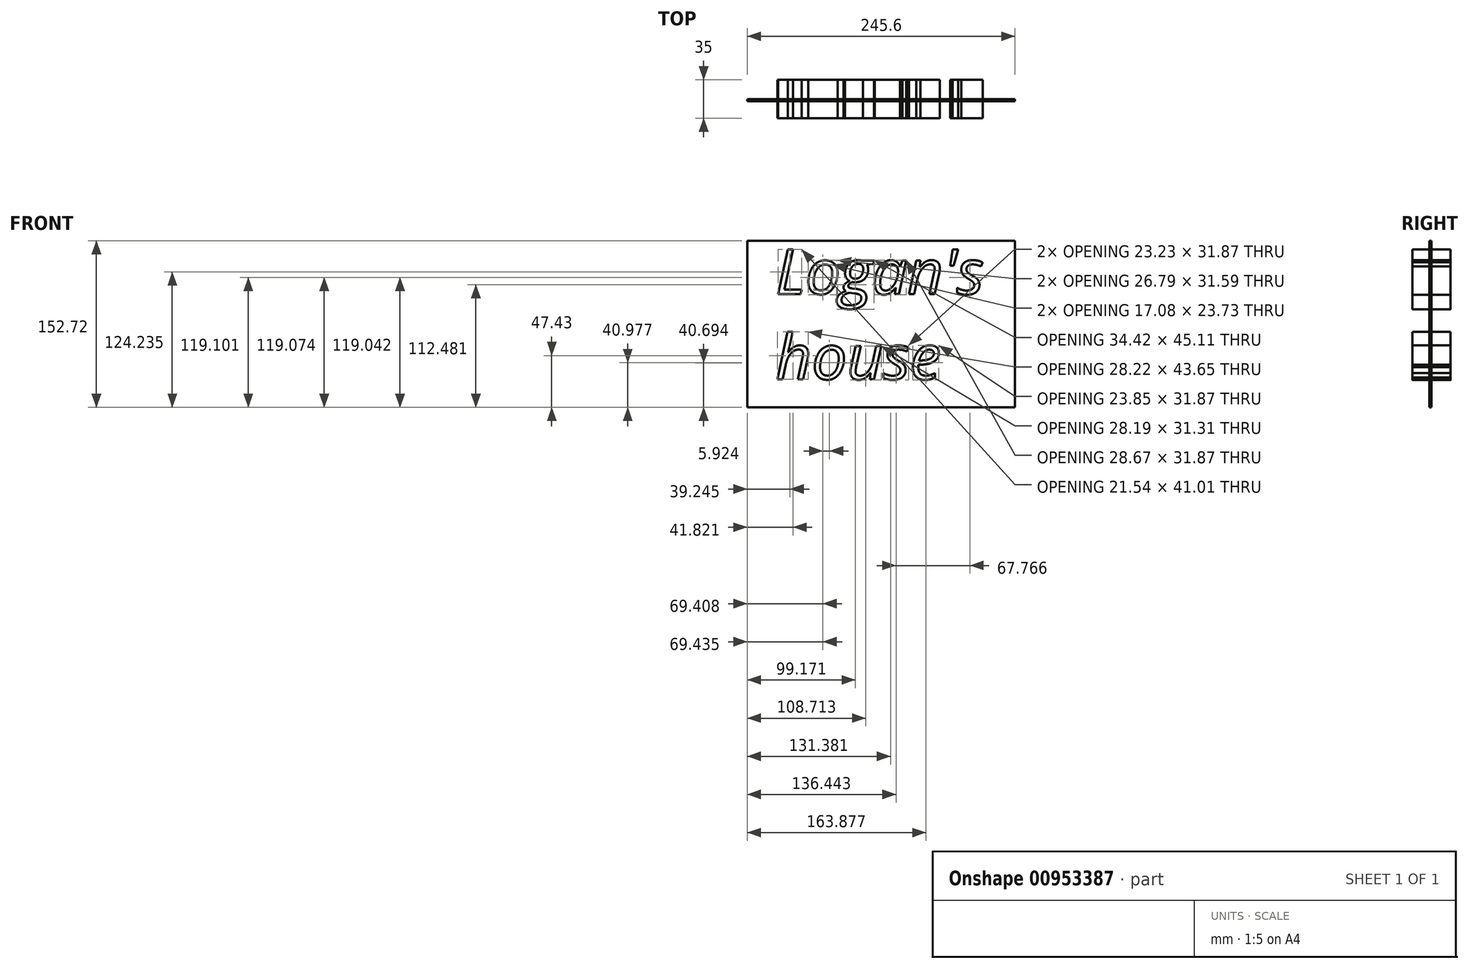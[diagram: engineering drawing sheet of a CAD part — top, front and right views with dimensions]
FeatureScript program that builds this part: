
annotation { "Feature Type Name" : "Feature", "Feature Type Description" : "" }
export const myFeature = defineFeature(function(context is Context, id is Id, definition is map)
    precondition{}
    {
        {
            var Q0;
            Q0=qCreatedBy(makeId("Front.planeOp"),FACE);
            var sketch = newSketch(context, id + "F0", { "sketchPlane" : qUnion([Q0])});
            skText(sketch, "E0", { "text": "Logan\'s \nhouse\n", "fontName": "OpenSans-Italic.ttf"});
            skLineSegment(sketch, "E1.bottom", {"start": v(122.8, -76.36) * mm, "end": v(-122.8, -76.36) * mm});
            skLineSegment(sketch, "E1.top", {"start": v(122.8, 76.36) * mm, "end": v(-122.8, 76.36) * mm});
            skLineSegment(sketch, "E1.left", {"start": v(122.8, -76.36) * mm, "end": v(122.8, 76.36) * mm});
            skLineSegment(sketch, "E1.right", {"start": v(-122.8, -76.36) * mm, "end": v(-122.8, 76.36) * mm});
            skPoint(sketch, "E1.middle", {"position": v(0, 0) * mm});
            const initialGuessF0  = {"E0": [-0.09674, 0.02737, 1, 0, 0.04136]};
            skSetInitialGuess(sketch, initialGuessF0);
            skSolve(sketch);
        }
        {
            var Q0;
            Q0=makeQuery(id+"F0.imprint","IMPRINT",FACE,{"disambiguationData":[TD([[makeQuery(id+"F0.imprint","IMPRINT",EDGE,{"derivedFrom":sQuery(id+"F0.wireOp",EDGE,"E0.sketch_text.stroke-0")}),-1.0]])]});
            var Q1;
            Q1=makeQuery(id+"F0.imprint","IMPRINT",FACE,{"disambiguationData":[TD([[makeQuery(id+"F0.imprint","IMPRINT",EDGE,{"derivedFrom":sQuery(id+"F0.wireOp",EDGE,"E0.sketch_text.stroke-6")}),-1.0]])]});
            var Q2;
            Q2=makeQuery(id+"F0.imprint","IMPRINT",FACE,{"disambiguationData":[TD([[makeQuery(id+"F0.imprint","IMPRINT",EDGE,{"derivedFrom":sQuery(id+"F0.wireOp",EDGE,"E0.sketch_text.stroke-26")}),-1.0]])]});
            var Q3;
            Q3=makeQuery(id+"F0.imprint","IMPRINT",FACE,{"disambiguationData":[TD([[makeQuery(id+"F0.imprint","IMPRINT",EDGE,{"derivedFrom":sQuery(id+"F0.wireOp",EDGE,"E0.sketch_text.stroke-72")}),-1.0]])]});
            var Q4;
            Q4=makeQuery(id+"F0.imprint","IMPRINT",FACE,{"disambiguationData":[TD([[makeQuery(id+"F0.imprint","IMPRINT",EDGE,{"derivedFrom":sQuery(id+"F0.wireOp",EDGE,"E0.sketch_text.stroke-97")}),-1.0]])]});
            var Q5;
            Q5=makeQuery(id+"F0.imprint","IMPRINT",FACE,{"disambiguationData":[TD([[makeQuery(id+"F0.imprint","IMPRINT",EDGE,{"derivedFrom":sQuery(id+"F0.wireOp",EDGE,"E0.sketch_text.stroke-117")}),-1.0]])]});
            var Q6;
            Q6=makeQuery(id+"F0.imprint","IMPRINT",FACE,{"disambiguationData":[TD([[makeQuery(id+"F0.imprint","IMPRINT",EDGE,{"derivedFrom":sQuery(id+"F0.wireOp",EDGE,"E0.sketch_text.stroke-121")}),-1.0]])]});
            extrude(context, id + "F1", {"entities" : qUnion([Q0, Q1, Q2, Q3, Q4, Q5, Q6]), "endBound" : BoundingType.SYMMETRIC, "depth" : 35 * mm, "offsetDistance" : 25 * mm});
        }
        {
            var Q0;
            Q0=makeQuery(id+"F0.imprint","IMPRINT",FACE,{"disambiguationData":[TD([[makeQuery(id+"F0.imprint","IMPRINT",EDGE,{"derivedFrom":sQuery(id+"F0.wireOp",EDGE,"E0.sketch_text.stroke-146")}),-1.0]])]});
            var Q1;
            Q1=makeQuery(id+"F0.imprint","IMPRINT",FACE,{"disambiguationData":[TD([[makeQuery(id+"F0.imprint","IMPRINT",EDGE,{"derivedFrom":sQuery(id+"F0.wireOp",EDGE,"E0.sketch_text.stroke-168")}),-1.0]])]});
            var Q2;
            Q2=makeQuery(id+"F0.imprint","IMPRINT",FACE,{"disambiguationData":[TD([[makeQuery(id+"F0.imprint","IMPRINT",EDGE,{"derivedFrom":sQuery(id+"F0.wireOp",EDGE,"E0.sketch_text.stroke-188")}),-1.0]])]});
            var Q3;
            Q3=makeQuery(id+"F0.imprint","IMPRINT",FACE,{"disambiguationData":[TD([[makeQuery(id+"F0.imprint","IMPRINT",EDGE,{"derivedFrom":sQuery(id+"F0.wireOp",EDGE,"E0.sketch_text.stroke-207")}),-1.0]])]});
            var Q4;
            Q4=makeQuery(id+"F0.imprint","IMPRINT",FACE,{"disambiguationData":[TD([[makeQuery(id+"F0.imprint","IMPRINT",EDGE,{"derivedFrom":sQuery(id+"F0.wireOp",EDGE,"E0.sketch_text.stroke-232")}),-1.0]])]});
            extrude(context, id + "F2", {"entities" : qUnion([Q0, Q1, Q2, Q3, Q4]), "endBound" : BoundingType.SYMMETRIC, "depth" : 35 * mm, "offsetDistance" : 25 * mm});
        }
        {
            var Q0;
            Q0=makeQuery(id+"F0.imprint","IMPRINT",FACE,{"disambiguationData":[TD([[makeQuery(id+"F0.imprint","IMPRINT",EDGE,{"derivedFrom":sQuery(id+"F0.wireOp",EDGE,"E0.sketch_text.stroke-0")}),1.0]])]});
            extrude(context, id + "F3", {"entities" : qUnion([Q0]), "depth" : 2 * mm, "offsetDistance" : 25 * mm});
        }
    });
